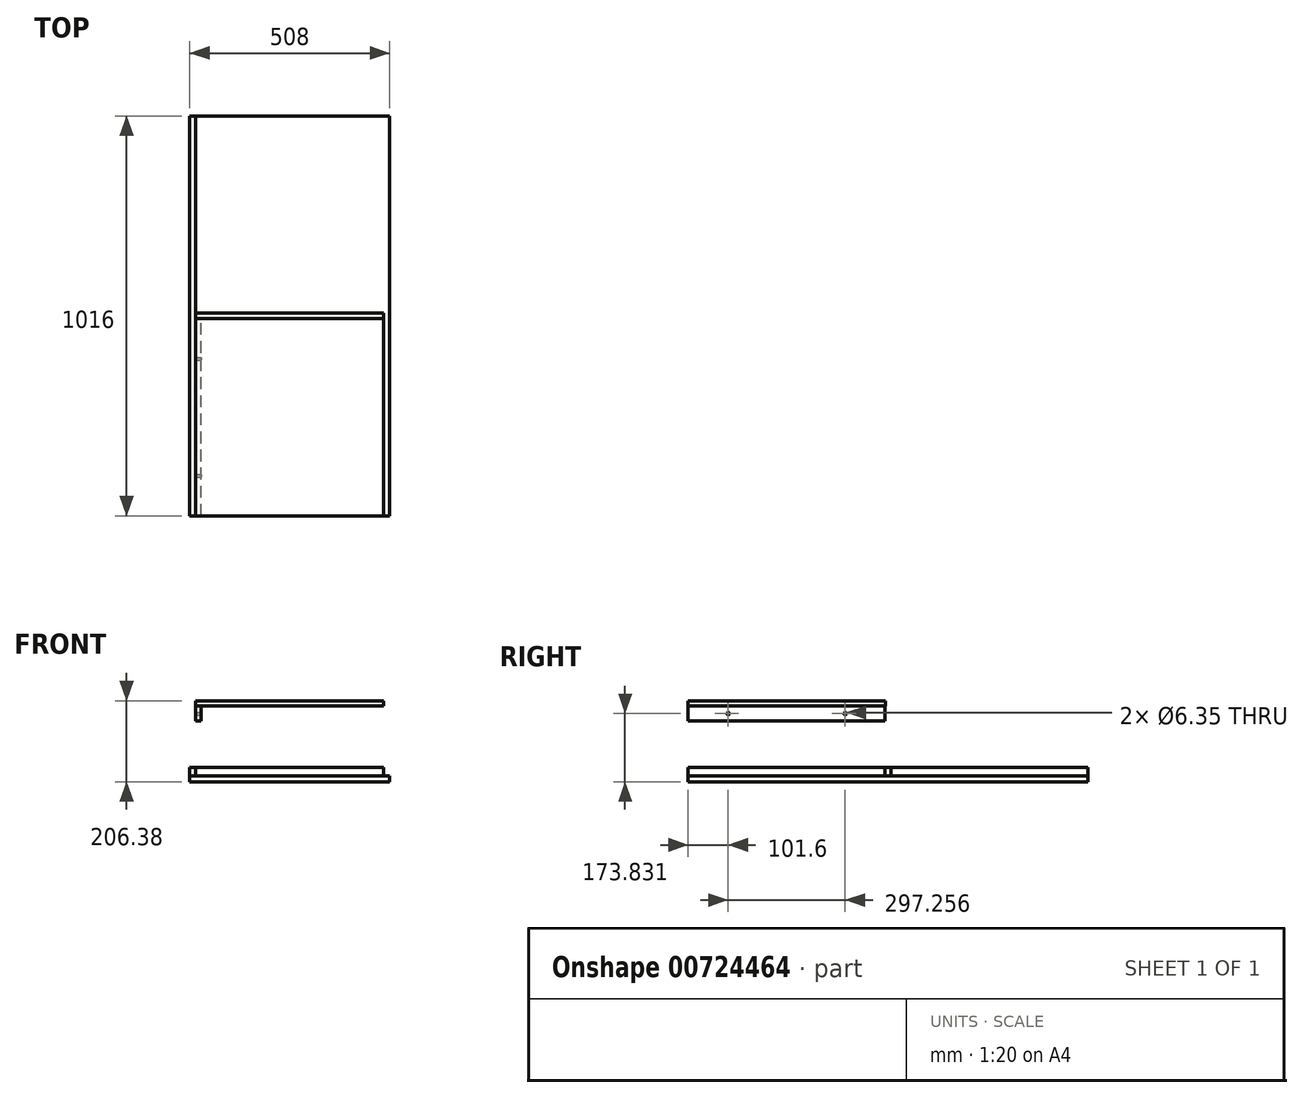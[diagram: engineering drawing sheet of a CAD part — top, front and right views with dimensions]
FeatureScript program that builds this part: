
annotation { "Feature Type Name" : "Feature", "Feature Type Description" : "" }
export const myFeature = defineFeature(function(context is Context, id is Id, definition is map)
    precondition{}
    {
        {
            var Q0;
            Q0=qCreatedBy(makeId("Top.planeOp"),FACE);
            var sketch = newSketch(context, id + "F0", { "sketchPlane" : qUnion([Q0])});
            skLineSegment(sketch, "E0.bottom", {"start": v(0, 0) * mm, "end": v(508, 0) * mm});
            skLineSegment(sketch, "E0.top", {"start": v(0, 1016) * mm, "end": v(508, 1016) * mm});
            skLineSegment(sketch, "E0.left", {"start": v(0, 0) * mm, "end": v(0, 1016) * mm});
            skLineSegment(sketch, "E0.right", {"start": v(508, 0) * mm, "end": v(508, 1016) * mm});
            skSolve(sketch);
        }
        {
            var Q0;
            Q0 = qSketchRegion(id + "F0", true);
            extrude(context, id + "F1", {"entities" : qUnion([Q0]), "depth" : 15.08 * mm, "offsetDistance" : 25.4 * mm});
        }
        {
            var Q0;
            Q0=makeQuery(id+"F1.opExtrude","CAP_FACE",FACE,{"disambiguationData":[OSD([sQuery(id+"F0.wireOp",EDGE,"E0.bottom"),sQuery(id+"F0.wireOp",EDGE,"E0.top"),sQuery(id+"F0.wireOp",EDGE,"E0.left"),sQuery(id+"F0.wireOp",EDGE,"E0.right")])],"isStart":false});
            var sketch = newSketch(context, id + "F2", { "sketchPlane" : qUnion([Q0])});
            skLineSegment(sketch, "E1.bottom", {"start": v(0, 0) * mm, "end": v(15.08, 0) * mm});
            skLineSegment(sketch, "E1.top", {"start": v(0, 1016) * mm, "end": v(15.08, 1016) * mm});
            skLineSegment(sketch, "E1.left", {"start": v(0, 0) * mm, "end": v(0, 1016) * mm});
            skLineSegment(sketch, "E1.right", {"start": v(15.08, 0) * mm, "end": v(15.08, 1016) * mm});
            skSolve(sketch);
        }
        {
            var Q0;
            Q0=makeQuery(id+"F2.imprint","IMPRINT",FACE,{"disambiguationData":[TD([[makeQuery(id+"F2.imprint","IMPRINT",EDGE,{"derivedFrom":sQuery(id+"F2.wireOp",EDGE,"E1.bottom")}),1.0]])]});
            extrude(context, id + "F3", {"entities" : qUnion([Q0]), "depth" : ((25 - (19 / 32 * 2)) - 2.5) * mm, "offsetDistance" : 25.4 * mm});
        }
        {
            var Q0;
            Q0=makeQuery(id+"F1.opExtrude","CAP_FACE",FACE,{"disambiguationData":[OSD([sQuery(id+"F0.wireOp",EDGE,"E0.bottom"),sQuery(id+"F0.wireOp",EDGE,"E0.top"),sQuery(id+"F0.wireOp",EDGE,"E0.left"),sQuery(id+"F0.wireOp",EDGE,"E0.right")])],"isStart":false});
            var sketch = newSketch(context, id + "F4", { "sketchPlane" : qUnion([Q0])});
            skLineSegment(sketch, "E2.bottom", {"start": v(492.92, 500.46) * mm, "end": v(15.08, 500.46) * mm});
            skLineSegment(sketch, "E2.top", {"start": v(492.92, 515.54) * mm, "end": v(15.08, 515.54) * mm});
            skLineSegment(sketch, "E2.left", {"start": v(492.92, 500.46) * mm, "end": v(492.92, 515.54) * mm});
            skLineSegment(sketch, "E2.right", {"start": v(15.08, 500.46) * mm, "end": v(15.08, 515.54) * mm});
            skSolve(sketch);
        }
        {
            var Q0;
            Q0=makeQuery(id+"F4.imprint","IMPRINT",FACE,{"disambiguationData":[TD([[makeQuery(id+"F4.imprint","IMPRINT",EDGE,{"derivedFrom":sQuery(id+"F4.wireOp",EDGE,"E2.bottom")}),-1.0]])]});
            var Q1;
            Q1=makeQuery(id+"F3.opExtrude","CAP_FACE",FACE,{"disambiguationData":[OSD([sQuery(id+"F2.wireOp",EDGE,"E1.bottom"),sQuery(id+"F2.wireOp",EDGE,"E1.top"),sQuery(id+"F2.wireOp",EDGE,"E1.left"),sQuery(id+"F2.wireOp",EDGE,"E1.right")])],"isStart":false});
            extrude(context, id + "F5", {"entities" : qUnion([Q0]), "endBound" : BoundingType.UP_TO_SURFACE, "depth" : 25.4 * mm, "endBoundEntityFace" : qUnion([Q1]), "offsetDistance" : 25.4 * mm});
        }
        {
            var Q0;
            Q0=makeQuery(id+"F3.opExtrude","SWEPT_FACE",FACE,{"disambiguationData":[OSD([sQuery(id+"F2.wireOp",EDGE,"E1.right")])]});
            var sketch = newSketch(context, id + "F6", { "sketchPlane" : qUnion([Q0])});
            skLineSegment(sketch, "E3.bottom", {"start": v(0, 154.78) * mm, "end": v(500.46, 154.78) * mm});
            skLineSegment(sketch, "E3.top", {"start": v(0, 192.88) * mm, "end": v(500.46, 192.88) * mm});
            skLineSegment(sketch, "E3.left", {"start": v(0, 154.78) * mm, "end": v(0, 192.88) * mm});
            skLineSegment(sketch, "E3.right", {"start": v(500.46, 154.78) * mm, "end": v(500.46, 192.88) * mm});
            skSolve(sketch);
        }
        {
            var Q0;
            Q0=makeQuery(id+"F6.imprint","IMPRINT",FACE,{"disambiguationData":[TD([[makeQuery(id+"F6.imprint","IMPRINT",EDGE,{"derivedFrom":sQuery(id+"F6.wireOp",EDGE,"E3.bottom")}),1.0]])]});
            extrude(context, id + "F7", {"entities" : qUnion([Q0]), "depth" : 13.5 * mm, "offsetDistance" : 25.4 * mm});
        }
        {
            var Q0;
            Q0=makeQuery(id+"F7.opExtrude","SWEPT_FACE",FACE,{"disambiguationData":[OSD([sQuery(id+"F6.wireOp",EDGE,"E3.top")])]});
            var sketch = newSketch(context, id + "F8", { "sketchPlane" : qUnion([Q0])});
            skLineSegment(sketch, "E4.bottom", {"start": v(15.08, 0) * mm, "end": v(492.9, 0) * mm});
            skLineSegment(sketch, "E4.top", {"start": v(15.08, 500.96) * mm, "end": v(492.9, 500.96) * mm});
            skLineSegment(sketch, "E4.left", {"start": v(15.08, 0) * mm, "end": v(15.08, 500.96) * mm});
            skLineSegment(sketch, "E4.right", {"start": v(492.9, 0) * mm, "end": v(492.9, 500.96) * mm});
            skSolve(sketch);
        }
        {
            var Q0;
            Q0 = qSketchRegion(id + "F8", true);
            extrude(context, id + "F9", {"entities" : qUnion([Q0]), "depth" : 13.5 * mm, "offsetDistance" : 25.4 * mm});
        }
        {
            var Q0;
            Q0=makeQuery(id+"F7.opExtrude","CAP_FACE",FACE,{"disambiguationData":[OSD([sQuery(id+"F6.wireOp",EDGE,"E3.bottom"),sQuery(id+"F6.wireOp",EDGE,"E3.top"),sQuery(id+"F6.wireOp",EDGE,"E3.left"),sQuery(id+"F6.wireOp",EDGE,"E3.right")])],"isStart":false});
            var sketch = newSketch(context, id + "F10", { "sketchPlane" : qUnion([Q0])});
            skCircle(sketch, "E5", {"center": v(101.6, 173.83) * mm, "radius": 3.18 * mm});
            skPoint(sketch, "E5.centerSnap0", {"position": v(0, 173.83) * mm});
            skCircle(sketch, "E6", {"center": v(398.86, 173.83) * mm, "radius": 3.18 * mm});
            skPoint(sketch, "E6.centerSnap0", {"position": v(500.46, 173.83) * mm});
            skSolve(sketch);
        }
        {
            var Q0;
            Q0 = qSketchRegion(id + "F10", true);
            extrude(context, id + "F11", {"entities" : qUnion([Q0]), "operationType" : NewBodyOperationType.REMOVE, "endBound" : BoundingType.THROUGH_ALL, "oppositeDirection" : true, "depth" : 25.4 * mm, "offsetDistance" : 25.4 * mm});
        }
        {
            var Q0;
            Q0=makeQuery(id+"F3.opExtrude","SWEPT_FACE",FACE,{"disambiguationData":[OSD([sQuery(id+"F2.wireOp",EDGE,"E1.right")])]});
            var sketch = newSketch(context, id + "F12", { "sketchPlane" : qUnion([Q0])});
            skCircle(sketch, "E7", {"center": v(101.6, 173.83) * mm, "radius": 3.18 * mm});
            skCircle(sketch, "E8", {"center": v(398.86, 173.83) * mm, "radius": 3.18 * mm});
            skCircle(sketch, "E9", {"center": v(101.6, 351.63) * mm, "radius": 3.18 * mm});
            skCircle(sketch, "E10", {"center": v(398.86, 351.63) * mm, "radius": 3.18 * mm});
            skLineSegment(sketch, "E11", {"start": v(508, 556.42) * mm, "end": v(508, 15.08) * mm, "construction": true});
            skCircle(sketch, "E12.MirrorC", {"center": v(617.14, 173.83) * mm, "radius": 3.18 * mm});
            skCircle(sketch, "E13.MirrorC", {"center": v(617.14, 351.63) * mm, "radius": 3.18 * mm});
            skCircle(sketch, "E14.MirrorC", {"center": v(914.4, 351.63) * mm, "radius": 3.18 * mm});
            skCircle(sketch, "E15.MirrorC", {"center": v(914.4, 173.83) * mm, "radius": 3.18 * mm});
            skSolve(sketch);
        }
        {
            var Q0;
            Q0 = qSketchRegion(id + "F12", true);
            extrude(context, id + "F13", {"entities" : qUnion([Q0]), "operationType" : NewBodyOperationType.REMOVE, "endBound" : BoundingType.THROUGH_ALL, "oppositeDirection" : true, "depth" : 25.4 * mm, "offsetDistance" : 25.4 * mm});
        }
    });
